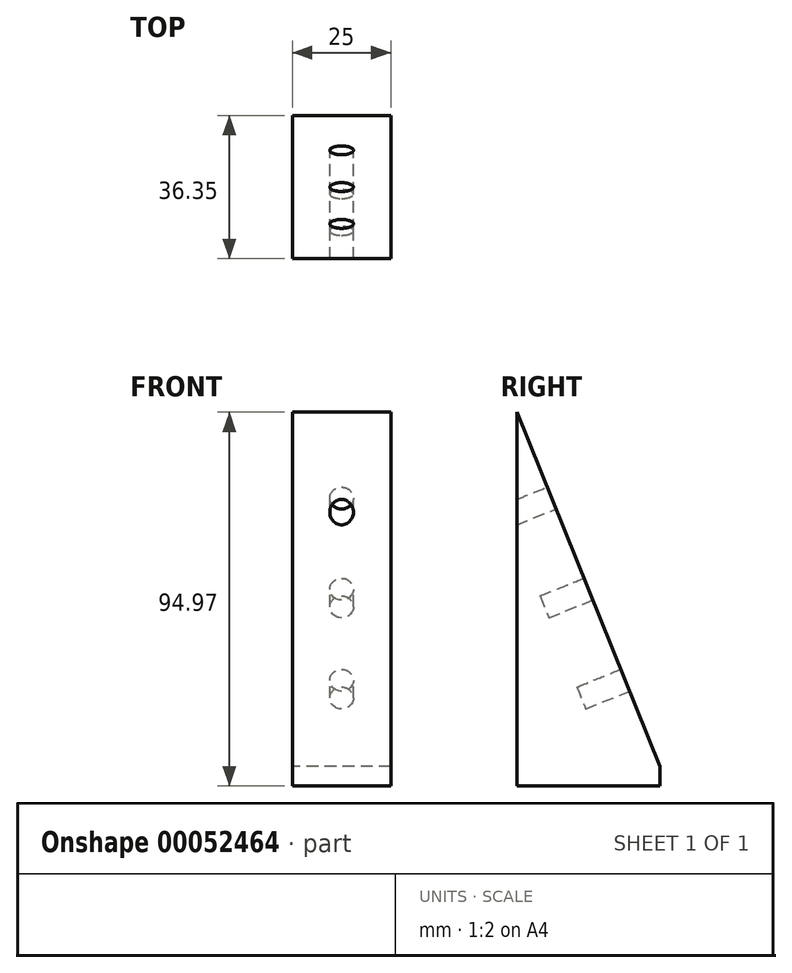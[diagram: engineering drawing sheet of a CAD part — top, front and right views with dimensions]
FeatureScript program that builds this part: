
annotation { "Feature Type Name" : "Feature", "Feature Type Description" : "" }
export const myFeature = defineFeature(function(context is Context, id is Id, definition is map)
    precondition{}
    {
        {
            var Q0;
            Q0=qCreatedBy(makeId("Right.planeOp"),FACE);
            var sketch = newSketch(context, id + "F0", { "sketchPlane" : qUnion([Q0])});
            skLineSegment(sketch, "E0", {"start": v(-116.71, 0) * mm, "end": v(122.35, 0) * mm, "construction": true});
            skLineSegment(sketch, "E1", {"start": v(0, 145.13) * mm, "end": v(0, -134.38) * mm, "construction": true});
            skLineSegment(sketch, "E2", {"start": v(0, 0) * mm, "end": v(0, 89.97) * mm});
            skLineSegment(sketch, "E3", {"start": v(0, 89.97) * mm, "end": v(36.35, 0) * mm});
            skLineSegment(sketch, "E4", {"start": v(36.35, 0) * mm, "end": v(0, 0) * mm});
            skLineSegment(sketch, "E5", {"start": v(36.35, 0) * mm, "end": v(36.35, 117.76) * mm, "construction": true});
            skSolve(sketch);
        }
        {
            var Q0;
            Q0 = qSketchRegion(id + "F0", true);
            extrude(context, id + "F1", {"entities" : qUnion([Q0]), "depth" : 25 * mm});
        }
        {
            var Q0;
            Q0=makeQuery(id+"F1.opExtrude","SWEPT_FACE",FACE,{"disambiguationData":[OSD([sQuery(id+"F0.wireOp",EDGE,"E4")])]});
            var sketch = newSketch(context, id + "F2", { "sketchPlane" : qUnion([Q0])});
            skLineSegment(sketch, "E6.bottom", {"start": v(0, 0) * mm, "end": v(25, 0) * mm});
            skLineSegment(sketch, "E6.top", {"start": v(0, -36.35) * mm, "end": v(25, -36.35) * mm});
            skLineSegment(sketch, "E6.left", {"start": v(0, 0) * mm, "end": v(0, -36.35) * mm});
            skLineSegment(sketch, "E6.right", {"start": v(25, 0) * mm, "end": v(25, -36.35) * mm});
            skSolve(sketch);
        }
        {
            var Q0;
            Q0 = qSketchRegion(id + "F2", true);
            extrude(context, id + "F3", {"entities" : qUnion([Q0]), "operationType" : NewBodyOperationType.ADD, "depth" : 5 * mm});
        }
        {
            var Q0;
            Q0=makeQuery(id+"F1.opExtrude","SWEPT_FACE",FACE,{"disambiguationData":[OSD([sQuery(id+"F0.wireOp",EDGE,"E3")])]});
            var sketch = newSketch(context, id + "F4", { "sketchPlane" : qUnion([Q0])});
            skLineSegment(sketch, "E7", {"start": v(-12.5, 91.87) * mm, "end": v(-12.5, -47.42) * mm, "construction": true});
            skPoint(sketch, "E7.startSnap0", {"position": v(-12.5, 83.42) * mm});
            skLineSegment(sketch, "E8", {"start": v(-32.35, 34.9) * mm, "end": v(9.38, 34.9) * mm, "construction": true});
            skPoint(sketch, "E8.startSnap0", {"position": v(-25, 34.9) * mm});
            skCircle(sketch, "E9", {"center": v(-12.5, 34.9) * mm, "radius": 3 * mm});
            skCircle(sketch, "E10", {"center": v(-12.5, 59.87) * mm, "radius": 3 * mm});
            skCircle(sketch, "E11.MirrorC", {"center": v(-12.5, 9.93) * mm, "radius": 3 * mm});
            skSolve(sketch);
        }
        {
            var Q0;
            Q0 = qSketchRegion(id + "F4", true);
            extrude(context, id + "F5", {"entities" : qUnion([Q0]), "operationType" : NewBodyOperationType.REMOVE, "oppositeDirection" : true, "depth" : 12 * mm});
        }
    });
